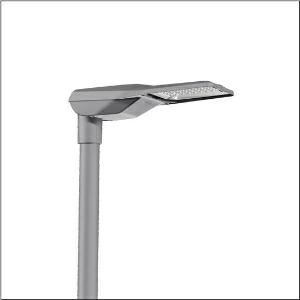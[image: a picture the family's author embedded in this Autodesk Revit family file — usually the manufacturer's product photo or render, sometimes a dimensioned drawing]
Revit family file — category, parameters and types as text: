
# Revit family: streetlight_sl_21_iq_mini___st0_5a_5xe2b31g08jb_3c5a
name_source: partatom
category: Lighting Fixtures
units: mm (PartAtom-declared; Revit-internal decimal feet)

## family parameters
Cut with Voids When Loaded = No
Host = Face
Light Source = No
Part Type = Normal
Room Calculation Point = No
Round Connector Dimension = Use Diameter
Shared = No

## types (1)
- --- (1 x LED, 10820 lm, 71.6 W, 3000K)
    Apparent Load = 72 VA
    CIE Flux Codes = 43 76 97 100 100
    Color Rendering = 70
    Color Temperature = 3000K
    Default Elevation = 1800 mm
    Description = Streetlight SL 21 iQ mini, mast luminaire, primary light control with lens, of PMMA, primary optical cover: cover, of toughened safety glass, transparent, light distribution: ST0.5a, light emission: direct distribution, primary light characteristic: asymmetric, installation type: post-top, side-entry, LED, High Power LED, rated luminous flux: 10.820lm, luminous efficacy: 151lm/W, light colour: 730, colour temperature: 3000K, control: Street-Remote, Auto-Match, Temp-Guard, Lumen-Switch, Night-Set, Smart-Wire, Light-Fading, Desk-Remote (wireless, voltage-free reading and setting of iQ features in the workshop via application-optimized NFC function/RFID function), optimised constant luminous flux control (CLO 2.0), presetting dimming linear, mains connection: 220..240V, AC, 50/60Hz, start of lifetime: 72W, end of service life: 75W, reduction: 33W, luminaire housing, of diecast aluminium, powder-coated, Siteco® metallic grey (DB 702S), corrosivity category C5 mid according to DIN EN ISO 12944, please order mast flange separately, inclination adjustable: 0°, 5°, 10°, 15°, sealing non-destructively replaceable, multi-level sealing system, length: 628mm, width: 235mm, height: 110mm, mast flange for spigot size: 42mm (side-entry): 5XC10008XM4, 60/48mm (side-entry/post-top): 5XC10108XM2, 76/60mm (side-entry/post-top): 5XC10108XM1, protection rating (complete): IP66, insulation class (complete): insulation class II (safety insulation), certification: CE, ENEC, ENEC+, VDE, impact resistance: IK09, permissible operating ambient temperature for outdoor applications: -40..+50°C, standard-compliant lighting for roads and squares, packaging unit: 1 piece

Light Distribution: ST0.5a
    Height = 110 mm
    Lamp = 1 x LED
    Lamp Light Flux = 10820 lm
    Lamp Power = 71.6 W
    Lamp count = 1
    Length = 625 mm
    Luminous efficacy = 151 lm/W
    Manufacturer = Siteco
    ModVariant = No
    Model = 5XE2B31G08JB
    Number of Poles = 1
    OnlyDefault = Yes
    Power Factor = 1
    Product Name = Streetlight SL 21 iQ mini | ST0.5a
    Product group = mast luminaire | pylon top
    ProductGroupID = 6100
    Protection Class = Protection class II
    Protection Degree = IP 66
    RLX_Detail_Level = 1
    RLX_Emergency_Light_Flux = 0 lm
    RLX_Emergency_Type = 0
    RLX_Emergency_Type_DB = No
    RlxData = <blob elided: 103473 chars, md5=286c8ae8>
    Socket = socket
    Standby Power = 0 W
    System Light Flux = 10820 lm
    System Power = 72 W
    Type Comments = factory setting: luminous flux: 100 % | dim-lin: 254 | 746 mA
    Type Image = l_1003519.jpg
    URL = http://relux.com
    VarID = @adj_104853
    Voltage = 0 V
    Weight = 0.00 kg
    Width = 234 mm

## geometry (parser evidence)
native form markers: Blend x4, Sweep x9
no freeform markers — native parametric forms only
